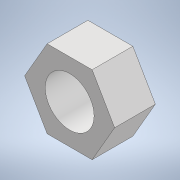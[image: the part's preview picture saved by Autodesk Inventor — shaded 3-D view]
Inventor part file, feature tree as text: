
AUTODESK INVENTOR PART (.ipt)
format: ipt  version: 2022 (Build 260153000, 153)  size: 100,864 bytes
history: native  units: in
note: dims shown in document units (in); Inventor stores cm internally (conversion verified against a paired STEP export)
features: extrude x1, sketch x1
ambient origin geometry x8: Origin, YZ Plane, XZ Plane, XY Plane, X Axis, Y Axis, Z Axis, Center Point
bodies: Solid1 (feature_tree)
feature tree (2):
  extrude  "Extrusion1"  Depth=0.1969in
  sketch  "Sketch1"  dims[d0=0.435in d1=0.2362in d2=0.1969in d3=0.0in]
